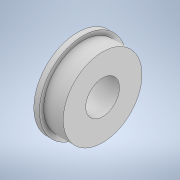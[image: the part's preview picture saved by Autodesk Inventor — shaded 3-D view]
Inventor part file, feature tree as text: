
AUTODESK INVENTOR PART (.ipt)
format: ipt  version: 2020.2 (Build 242310000, 310)  size: 125,952 bytes
history: native  units: in
note: dims shown in document units (in); Inventor stores cm internally (conversion verified against a paired STEP export)
features: revolve x1
ambient origin geometry x8: Origin, YZ Plane, XZ Plane, XY Plane, X Axis, Y Axis, Z Axis, Center Point
bodies: Solid1 (feature_tree)
feature tree (1):
  revolve  "Revolve1"  [1 undecoded]
note: 1 required parameter value undecoded (feature->parameter linkage not recoverable at this tier; creation-order binding heuristic only, values carry confidence <= 0.55)
